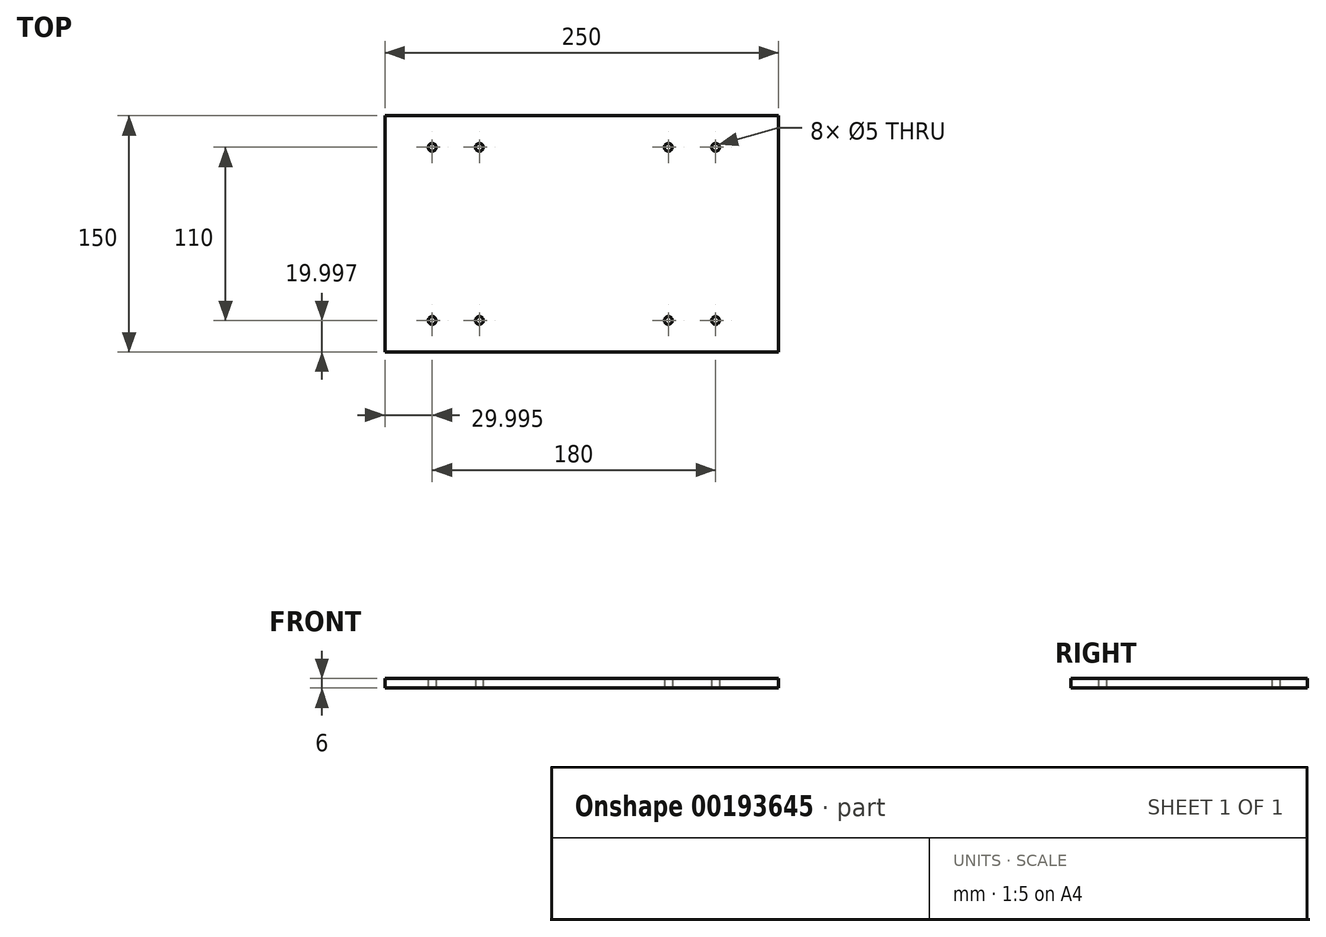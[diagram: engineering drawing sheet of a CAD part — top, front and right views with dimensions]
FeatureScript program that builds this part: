
annotation { "Feature Type Name" : "Feature", "Feature Type Description" : "" }
export const myFeature = defineFeature(function(context is Context, id is Id, definition is map)
    precondition{}
    {
        {
            var Q0;
            Q0=qCreatedBy(makeId("Top.planeOp"),FACE);
            var sketch = newSketch(context, id + "F0", { "sketchPlane" : qUnion([Q0])});
            skLineSegment(sketch, "E0.bottom", {"start": v(-185.24, 81.1) * mm, "end": v(64.76, 81.1) * mm});
            skLineSegment(sketch, "E0.top", {"start": v(-185.24, -68.9) * mm, "end": v(64.76, -68.9) * mm});
            skLineSegment(sketch, "E0.left", {"start": v(-185.24, 81.1) * mm, "end": v(-185.24, -68.9) * mm});
            skLineSegment(sketch, "E0.right", {"start": v(64.76, 81.1) * mm, "end": v(64.76, -68.9) * mm});
            skCircle(sketch, "E1", {"center": v(-125.24, 61.1) * mm, "radius": 2.5 * mm});
            skCircle(sketch, "E2", {"center": v(-155.24, 61.1) * mm, "radius": 2.5 * mm});
            skCircle(sketch, "E3", {"center": v(24.76, 61.1) * mm, "radius": 2.5 * mm});
            skCircle(sketch, "E4", {"center": v(-5.24, 61.1) * mm, "radius": 2.5 * mm});
            skCircle(sketch, "E5", {"center": v(-155.24, -48.9) * mm, "radius": 2.5 * mm});
            skCircle(sketch, "E6", {"center": v(-125.24, -48.9) * mm, "radius": 2.5 * mm});
            skCircle(sketch, "E7", {"center": v(-5.24, -48.9) * mm, "radius": 2.5 * mm});
            skCircle(sketch, "E8", {"center": v(24.76, -48.9) * mm, "radius": 2.5 * mm});
            skSolve(sketch);
        }
        {
            var Q0;
            Q0=makeQuery(id+"F0.imprint","IMPRINT",FACE,{"disambiguationData":[TD([[makeQuery(id+"F0.imprint","IMPRINT",EDGE,{"derivedFrom":sQuery(id+"F0.wireOp",EDGE,"E0.bottom")}),-1.0]])]});
            extrude(context, id + "F1", {"entities" : qUnion([Q0]), "depth" : 6 * mm});
        }
    });
